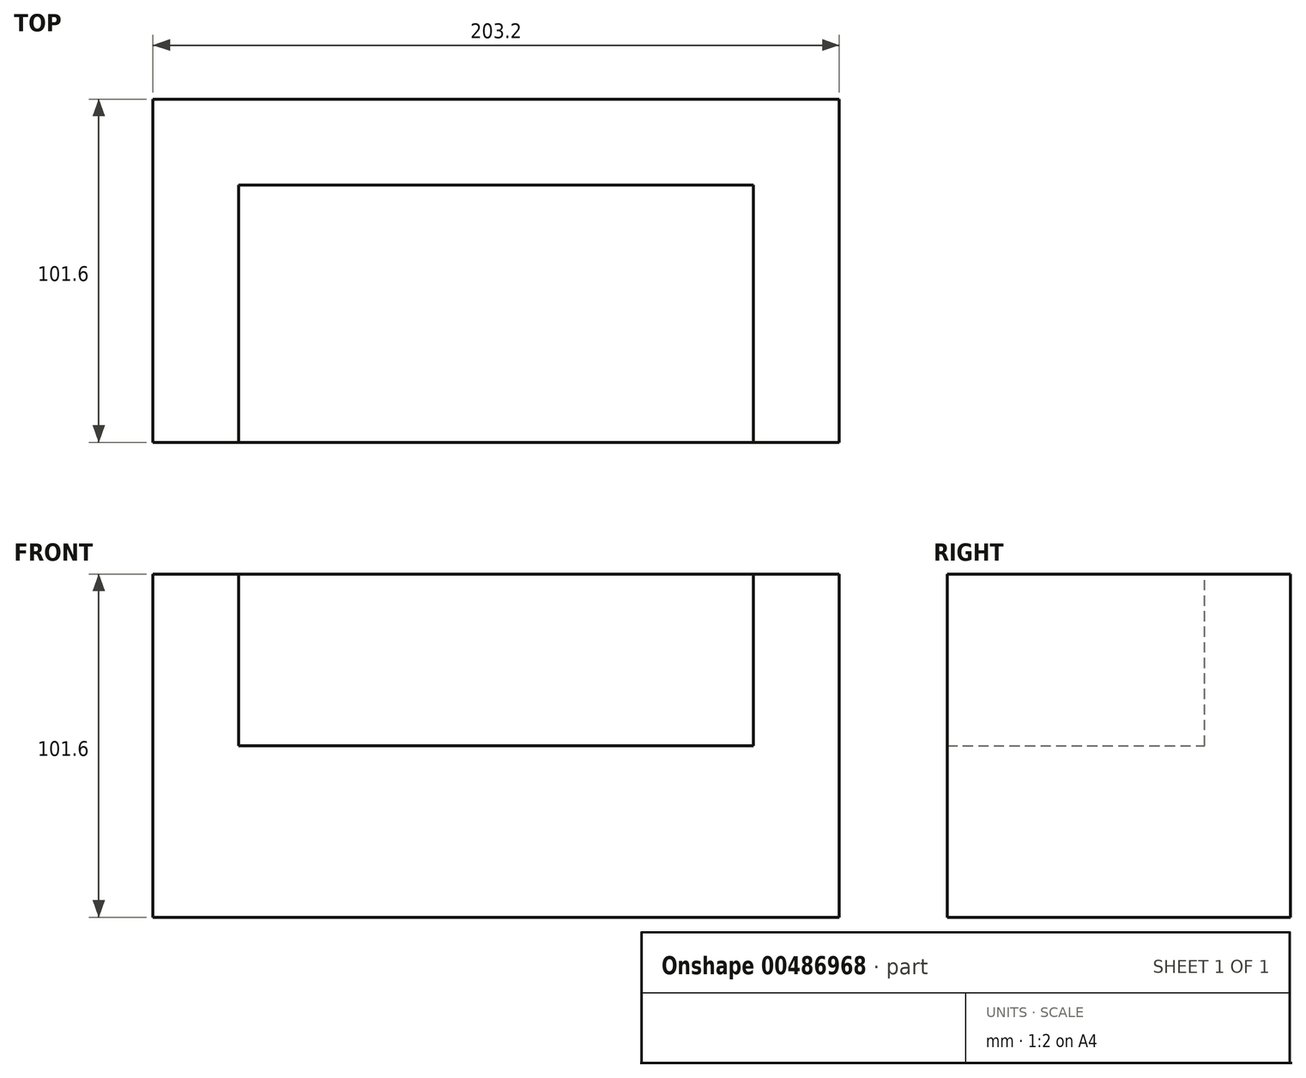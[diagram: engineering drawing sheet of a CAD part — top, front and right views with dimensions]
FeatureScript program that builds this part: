
annotation { "Feature Type Name" : "Feature", "Feature Type Description" : "" }
export const myFeature = defineFeature(function(context is Context, id is Id, definition is map)
    precondition{}
    {
        {
            var Q0;
            Q0=qCreatedBy(makeId("Front.planeOp"),FACE);
            var sketch = newSketch(context, id + "F0", { "sketchPlane" : qUnion([Q0])});
            skLineSegment(sketch, "E0.bottom", {"start": v(0, 0) * mm, "end": v(-203.2, 0) * mm});
            skLineSegment(sketch, "E0.top", {"start": v(0, 101.6) * mm, "end": v(-203.2, 101.6) * mm});
            skLineSegment(sketch, "E0.left", {"start": v(0, 0) * mm, "end": v(0, 101.6) * mm});
            skLineSegment(sketch, "E0.right", {"start": v(-203.2, 0) * mm, "end": v(-203.2, 101.6) * mm});
            skSolve(sketch);
        }
        {
            var Q0;
            Q0=makeQuery(id+"F0.imprint","IMPRINT",FACE,{"disambiguationData":[TD([[makeQuery(id+"F0.imprint","IMPRINT",EDGE,{"derivedFrom":sQuery(id+"F0.wireOp",EDGE,"E0.bottom")}),-1.0]])]});
            extrude(context, id + "F1", {"entities" : qUnion([Q0]), "depth" : 101.6 * mm});
        }
        {
            var Q0;
            Q0=makeQuery(id+"F1.opExtrude","CAP_FACE",FACE,{"disambiguationData":[OSD([sQuery(id+"F0.wireOp",EDGE,"E0.bottom"),sQuery(id+"F0.wireOp",EDGE,"E0.top"),sQuery(id+"F0.wireOp",EDGE,"E0.left"),sQuery(id+"F0.wireOp",EDGE,"E0.right")])],"isStart":false});
            var sketch = newSketch(context, id + "F2", { "sketchPlane" : qUnion([Q0])});
            skLineSegment(sketch, "E1.bottom", {"start": v(-177.8, 0) * mm, "end": v(-25.4, 0) * mm});
            skLineSegment(sketch, "E1.top", {"start": v(-177.8, 76.2) * mm, "end": v(-25.4, 76.2) * mm});
            skLineSegment(sketch, "E1.left", {"start": v(-177.8, 0) * mm, "end": v(-177.8, 76.2) * mm});
            skLineSegment(sketch, "E1.right", {"start": v(-25.4, 0) * mm, "end": v(-25.4, 76.2) * mm});
            skSolve(sketch);
        }
        {
            var Q0;
            Q0=makeQuery(id+"F2.imprint","IMPRINT",FACE,{"disambiguationData":[TD([[makeQuery(id+"F2.imprint","IMPRINT",EDGE,{"derivedFrom":sQuery(id+"F2.wireOp",EDGE,"E1.bottom")}),-1.0]])]});
            extrude(context, id + "F3", {"entities" : qUnion([Q0]), "operationType" : NewBodyOperationType.REMOVE, "oppositeDirection" : true, "depth" : 50.8 * mm});
        }
        {
            var Q0;
            Q0=makeQuery(id+"F1.opExtrude","SWEPT_BODY",BODY,{"disambiguationData":[OSD([sQuery(id+"F0.wireOp",EDGE,"E0.bottom"),sQuery(id+"F0.wireOp",EDGE,"E0.top"),sQuery(id+"F0.wireOp",EDGE,"E0.left"),sQuery(id+"F0.wireOp",EDGE,"E0.right")])]});
            var Q1;
            Q1=makeQuery(id+"F1.opExtrude","CAP_EDGE",EDGE,{"disambiguationData":[OSD([sQuery(id+"F0.wireOp",EDGE,"E0.top")])],"isStart":false});
            transform(context, id + "F4", {"entities" : qUnion([Q0]), "transformType" : TransformType.ROTATION, "transformAxis" : qUnion([Q1]), "angle" : 90 * degree, "makeCopy" : false});
        }
    });
